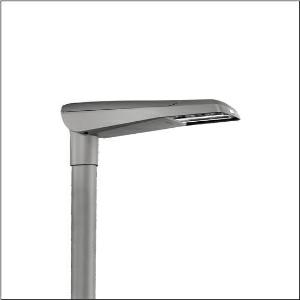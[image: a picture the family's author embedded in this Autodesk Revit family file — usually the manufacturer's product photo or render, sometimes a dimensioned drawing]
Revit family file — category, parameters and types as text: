
# Revit family: streetlight_sl_11_iq_micro___st1_0ab_5xc1nc1f08ce_393e
name_source: partatom
category: Lighting Fixtures
units: mm (PartAtom-declared; Revit-internal decimal feet)

## family parameters
Cut with Voids When Loaded = No
Host = Face
Light Source = No
Part Type = Normal
Room Calculation Point = No
Round Connector Dimension = Use Diameter
Shared = No

## types (1)
- --- (1 x LED, 1280 lm, 14 W, 2200K)
    Apparent Load = 14 VA
    CIE Flux Codes = 29 63 95 100 100
    Color Rendering = 70
    Color Temperature = 2200K
    Default Elevation = 1800 mm
    Description = Streetlight SL 11 iQ micro, mast luminaire, primary light control with 3 zone facetted reflector, of plastic, silver coated, highly specular, primary optical cover: cover, of PMMA, transparent, light distribution: ST1.0aB, light emission: direct distribution, primary light characteristic: asymmetric, installation type: post-top, side-entry, lamps: LED, High Power LED, rated values: 1.500lm | 13,8W | 108,7lm/W (begin service life); end service life: 1.500lm | 14W; at 50% lumin. flux: 750lm | 7,5W | 100lm/W, colour temperature: 2200/2700/3000/4000K, colour rendering: CRI > 70, light colour: 722/727/730/740, light setting 1 begin service life: 100% | 1.500lm | 13,8W | 108,7lm/W | 3.000K, light setting 1 end service life: 14W, further light settings possible, control: Street-Remote, Auto-Match, Temp-Guard, Lumen-Switch, Night-Set, Smart-Wire, Light-Fading, Desk-Remote (wireless, voltage-free reading and setting of iQ features in the workshop via application-optimized NFC function/RFID function), optimised constant luminous flux control (CLO 2.0), with cable H07RN-F 3x 1.5mm², mains connection: 220..240V, AC, 50/60Hz, connection cable pre-assembled, cable length: 5,5m, luminaire housing, of diecast aluminium, powder-coated, SITECO metallic grey (DB 702S), please order mast flange separately, inclination adjustable without tools: 0°, 5°, 10°, 15° (post-top) | 0°, -5°, -10°, -15° (side-entry), sealing non-destructively replaceable, multi-level sealing system, length: 600mm, width: 174mm, height: 116mm, mast flange for spigot size: 42mm (side-entry): 5XC10008XM4, 60/48mm (side-entry/post-top): 5XC10108XM2, 76/60mm (side-entry/post-top): 5XC10108XM1, equipment: standard, protection rating (complete): IP66, insulation class (complete): insulation class II (safety insulation), certification: CE, ENEC, ENEC+, VDE, impact resistance: IK10, permissible operating ambient temperature for outdoor applications: -25..+50°C, standard-compliant lighting for roads and squares, Environmental Product Declaration (EPD) tested and certified by an independent institute, packaging unit: 1 piece

Light Distribution: ST1.0aB
    Height = 116 mm
    Lamp = 1 x LED
    Lamp Light Flux = 1280 lm
    Lamp Power = 14 W
    Lamp count = 1
    Length = 600 mm
    Luminous efficacy = 91 lm/W
    Manufacturer = Siteco
    ModVariant = No
    Model = 5XC1NC1F08CE
    Mounting Place = Pole
    Mounting Type = Pole top
    Number of Poles = 1
    OnlyDefault = Yes
    Power Factor = 1
    Product Name = Streetlight SL 11 iQ micro | ST1.0aB
    Product group = mast luminaire | pylon top
    ProductGroupID = 6100
    Protection Class = Protection class II
    Protection Degree = IP 66
    RLX_Detail_Level = 1
    RLX_Emergency_Light_Flux = 0 lm
    RLX_Emergency_Type = 0
    RLX_Emergency_Type_DB = No
    RlxData = <blob elided: 57913 chars, md5=7b2a341a>
    Socket = socket
    Standby Power = 0 W
    System Light Flux = 1280 lm
    System Power = 14 W
    Type Comments = individual setting: luminous flux: 100 % | dim-lin: 254 | 369 mA
    Type Image = l_1006566.jpg
    URL = http://relux.com
    VarID = @adj_022985
    Voltage = 0 V
    Weight = 0.00 kg
    Width = 174 mm

## geometry (parser evidence)
native form markers: Blend x4, Sweep x11
no freeform markers — native parametric forms only
